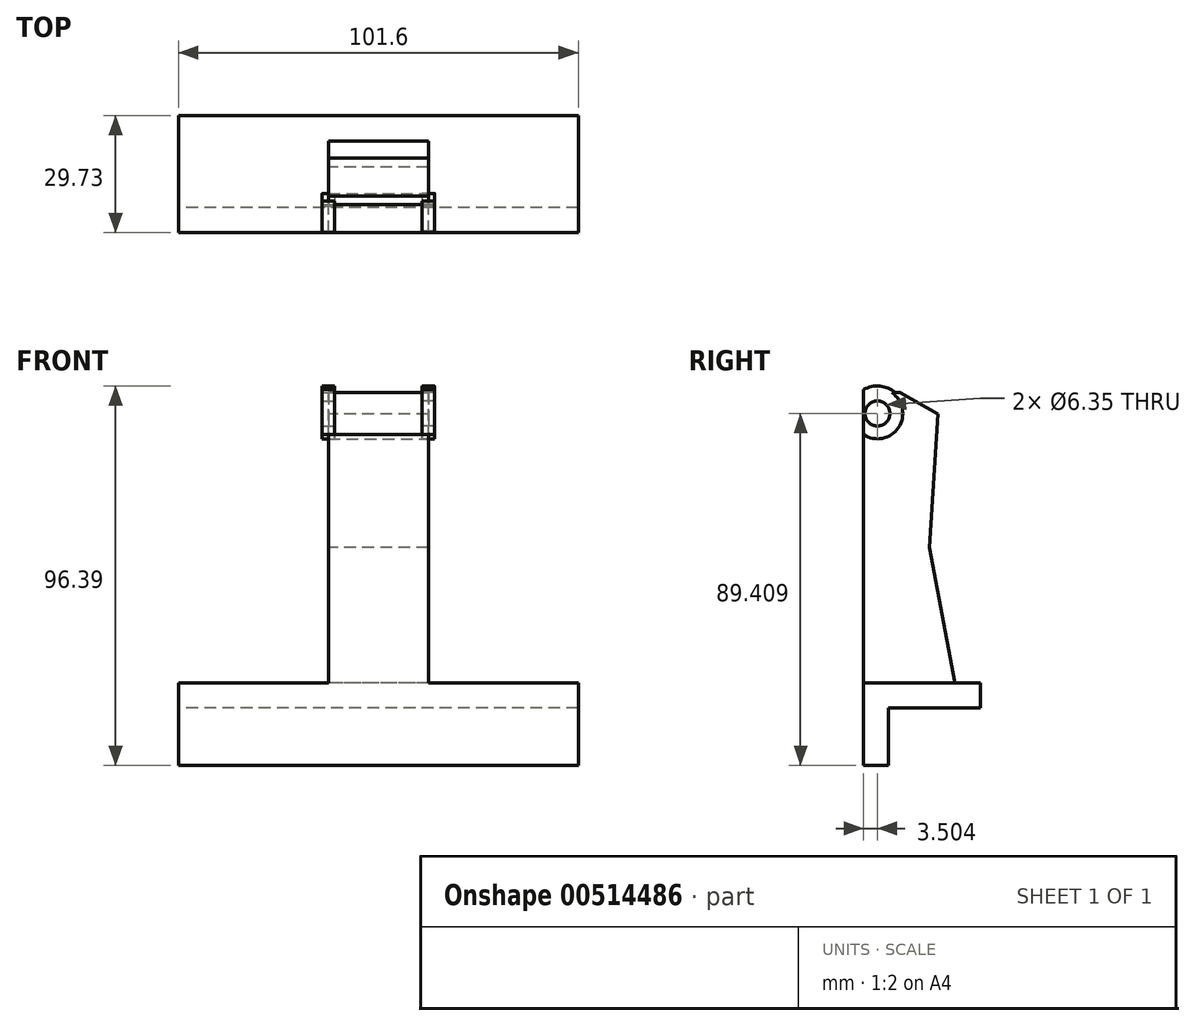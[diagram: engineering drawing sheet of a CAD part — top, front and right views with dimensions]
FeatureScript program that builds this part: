
annotation { "Feature Type Name" : "Feature", "Feature Type Description" : "" }
export const myFeature = defineFeature(function(context is Context, id is Id, definition is map)
    precondition{}
    {
        {
            var Q0;
            Q0=qCreatedBy(makeId("Right.planeOp"),FACE);
            var sketch = newSketch(context, id + "F0", { "sketchPlane" : qUnion([Q0])});
            skLineSegment(sketch, "E0.bottom", {"start": v(0, 0) * mm, "end": v(6.35, 0) * mm});
            skLineSegment(sketch, "E0.left", {"start": v(0, 0) * mm, "end": v(0, 20.91) * mm});
            skLineSegment(sketch, "E0.right", {"start": v(6.35, 0) * mm, "end": v(6.35, 14.56) * mm});
            skLineSegment(sketch, "E1.top", {"start": v(6.35, 14.56) * mm, "end": v(23.38, 14.56) * mm});
            skLineSegment(sketch, "E1.left", {"start": v(0, 20.91) * mm, "end": v(0, 14.56) * mm});
            skLineSegment(sketch, "E1.right", {"start": v(23.38, 20.91) * mm, "end": v(23.38, 14.56) * mm});
            skLineSegment(sketch, "E2.bottom", {"start": v(12.7, 14.56) * mm, "end": v(6.35, 14.56) * mm});
            skLineSegment(sketch, "E2.top", {"start": v(12.7, 101.1) * mm, "end": v(0, 101.1) * mm});
            skLineSegment(sketch, "E2.right", {"start": v(0, 20.91) * mm, "end": v(0, 101.1) * mm});
            skLineSegment(sketch, "E3", {"start": v(12.7, 65.87) * mm, "end": v(23.38, 20.91) * mm});
            skLineSegment(sketch, "E4", {"start": v(0, 20.91) * mm, "end": v(23.38, 20.91) * mm});
            skLineSegment(sketch, "E5", {"start": v(12.7, 101.1) * mm, "end": v(19.3, 97.56) * mm});
            skLineSegment(sketch, "E6", {"start": v(19.3, 97.56) * mm, "end": v(19.3, 74.64) * mm});
            skLineSegment(sketch, "E7", {"start": v(19.3, 74.64) * mm, "end": v(12.7, 65.87) * mm});
            skSolve(sketch);
        }
        {
            var Q0;
            Q0=makeQuery(id+"F0.imprint","IMPRINT",FACE,{"disambiguationData":[TD([[makeQuery(id+"F0.imprint","IMPRINT",EDGE,{"derivedFrom":sQuery(id+"F0.wireOp",EDGE,"E0.bottom")}),1.0]])]});
            extrude(context, id + "F1", {"entities" : qUnion([Q0]), "depth" : 101.6 * mm});
        }
        {
            var Q0;
            Q0=makeQuery(id+"F1.opExtrude","CAP_FACE",FACE,{"disambiguationData":[OSD([sQuery(id+"F0.wireOp",EDGE,"E0.bottom"),sQuery(id+"F0.wireOp",EDGE,"E0.left"),sQuery(id+"F0.wireOp",EDGE,"E0.right"),sQuery(id+"F0.wireOp",EDGE,"E1.top"),sQuery(id+"F0.wireOp",EDGE,"E1.left"),sQuery(id+"F0.wireOp",EDGE,"E1.right"),sQuery(id+"F0.wireOp",EDGE,"E2.bottom"),sQuery(id+"F0.wireOp",EDGE,"E4")])],"isStart":false});
            cPlane(context, id + "F2", {"entities" : qUnion([Q0]), "cplaneType" : CPlaneType.OFFSET, "offset" : 50.8 * mm, "oppositeDirection" : true, "width" : 152.4 * mm, "height" : 152.4 * mm});
        }
        {
            var Q0;
            Q0=qCreatedBy(id+"F2.planeOp",FACE);
            var sketch = newSketch(context, id + "F3", { "sketchPlane" : qUnion([Q0])});
            skLineSegment(sketch, "E8", {"start": v(0, 18.54) * mm, "end": v(0, 94.71) * mm});
            skLineSegment(sketch, "E9", {"start": v(0, 94.71) * mm, "end": v(9.23, 94.71) * mm});
            skLineSegment(sketch, "E10", {"start": v(16.68, 55.42) * mm, "end": v(23.22, 20.92) * mm});
            skLineSegment(sketch, "E11", {"start": v(23.22, 20.92) * mm, "end": v(19.9, 16.72) * mm});
            skLineSegment(sketch, "E12", {"start": v(19.9, 16.72) * mm, "end": v(0, 18.54) * mm});
            skLineSegment(sketch, "E13", {"start": v(9.23, 94.71) * mm, "end": v(18.9, 89.31) * mm});
            skLineSegment(sketch, "E14", {"start": v(18.9, 89.31) * mm, "end": v(16.68, 55.42) * mm});
            skSolve(sketch);
        }
        {
            var Q0;
            Q0=makeQuery(id+"F3.imprint","IMPRINT",FACE,{"disambiguationData":[TD([[makeQuery(id+"F3.imprint","IMPRINT",EDGE,{"derivedFrom":sQuery(id+"F3.wireOp",EDGE,"E8")}),-1.0]])]});
            extrude(context, id + "F4", {"entities" : qUnion([Q0]), "operationType" : NewBodyOperationType.ADD, "depth" : 12.7 * mm, "hasSecondDirection" : true, "secondDirectionOppositeDirection" : true, "secondDirectionDepth" : 12.7 * mm});
        }
        {
            var Q0;
            Q0=makeQuery(id+"F4.opExtrude","CAP_FACE",FACE,{"disambiguationData":[OSD([sQuery(id+"F3.wireOp",EDGE,"E8"),sQuery(id+"F3.wireOp",EDGE,"E9"),sQuery(id+"F3.wireOp",EDGE,"E10"),sQuery(id+"F3.wireOp",EDGE,"E11"),sQuery(id+"F3.wireOp",EDGE,"E12")])],"isStart":false});
            var sketch = newSketch(context, id + "F5", { "sketchPlane" : qUnion([Q0])});
            skCircle(sketch, "E15", {"center": v(3.5, 89.4) * mm, "radius": 6.43 * mm});
            skSolve(sketch);
        }
        {
            var Q0;
            {var subQ0=sQuery(id+"F5.wireOp",EDGE,"E15");var subQ1=makeQuery(id+"F4.opExtrude","CAP_EDGE",EDGE,{"disambiguationData":[OSD([sQuery(id+"F3.wireOp",EDGE,"E9")])],"isStart":false});var subQ2=makeQuery(id+"F5.imprint","INTERSECT",VERTEX,{"derivedFrom":[subQ1,subQ0]});Q0=makeQuery(id+"F5.imprint","IMPRINT",FACE,{"disambiguationData":[TD([[makeQuery(id+"F5.imprint","IMPRINT",EDGE,{"disambiguationData":[TD([[subQ2,-1.0]])],"derivedFrom":subQ0}),1.0]])]});}
            var Q1;
            {var subQ0=sQuery(id+"F5.wireOp",EDGE,"E15");var subQ1=makeQuery(id+"F4.opExtrude","CAP_EDGE",EDGE,{"disambiguationData":[OSD([sQuery(id+"F3.wireOp",EDGE,"E9")])],"isStart":false});var subQ2=makeQuery(id+"F5.imprint","INTERSECT",VERTEX,{"derivedFrom":[subQ1,subQ0]});Q1=makeQuery(id+"F5.imprint","IMPRINT",FACE,{"disambiguationData":[TD([[makeQuery(id+"F5.imprint","IMPRINT",EDGE,{"disambiguationData":[TD([[subQ2,1.0]])],"derivedFrom":subQ0}),1.0]])]});}
            extrude(context, id + "F6", {"entities" : qUnion([Q0, Q1]), "operationType" : NewBodyOperationType.REMOVE, "oppositeDirection" : true, "depth" : 25.4 * mm});
        }
        {
            var Q0;
            Q0=makeQuery(id+"F1.opExtrude","SWEPT_FACE",FACE,{"disambiguationData":[OSD([sQuery(id+"F0.wireOp",EDGE,"E1.right")])]});
            extrude(context, id + "F7", {"entities" : qUnion([Q0]), "operationType" : NewBodyOperationType.ADD, "depth" : 6.35 * mm});
        }
        {
            var Q0;
            Q0=makeQuery(id+"F4.opExtrude","CAP_FACE",FACE,{"disambiguationData":[OSD([sQuery(id+"F3.wireOp",EDGE,"E8"),sQuery(id+"F3.wireOp",EDGE,"E9"),sQuery(id+"F3.wireOp",EDGE,"E10"),sQuery(id+"F3.wireOp",EDGE,"E11"),sQuery(id+"F3.wireOp",EDGE,"E12"),sQuery(id+"F3.wireOp",EDGE,"E13"),sQuery(id+"F3.wireOp",EDGE,"E14")])],"isStart":false});
            var sketch = newSketch(context, id + "F8", { "sketchPlane" : qUnion([Q0])});
            skCircle(sketch, "E16", {"center": v(3.5, 89.4) * mm, "radius": 6.99 * mm});
            skCircle(sketch, "E17", {"center": v(3.5, 89.4) * mm, "radius": 3.18 * mm});
            skSolve(sketch);
        }
        {
            var Q0;
            Q0=makeQuery(id+"F4.opExtrude","CAP_FACE",FACE,{"disambiguationData":[OSD([sQuery(id+"F3.wireOp",EDGE,"E8"),sQuery(id+"F3.wireOp",EDGE,"E9"),sQuery(id+"F3.wireOp",EDGE,"E10"),sQuery(id+"F3.wireOp",EDGE,"E11"),sQuery(id+"F3.wireOp",EDGE,"E12"),sQuery(id+"F3.wireOp",EDGE,"E13"),sQuery(id+"F3.wireOp",EDGE,"E14")])],"isStart":true});
            var sketch = newSketch(context, id + "F9", { "sketchPlane" : qUnion([Q0])});
            skCircle(sketch, "E18", {"center": v(-3.5, 89.4) * mm, "radius": 6.98 * mm});
            skCircle(sketch, "E19", {"center": v(-3.5, 89.4) * mm, "radius": 3.18 * mm});
            skSolve(sketch);
        }
        {
            var Q0;
            Q0=makeQuery(id+"F9.imprint","IMPRINT",FACE,{"disambiguationData":[TD([[makeQuery(id+"F9.imprint","IMPRINT",EDGE,{"derivedFrom":sQuery(id+"F9.wireOp",EDGE,"E19")}),-1.0]])]});
            extrude(context, id + "F10", {"entities" : qUnion([Q0]), "endBound" : BoundingType.SYMMETRIC, "depth" : 3.17 * mm, "offsetDistance" : 25.4 * mm});
        }
        {
            var Q0;
            Q0=makeQuery(id+"F8.imprint","IMPRINT",FACE,{"disambiguationData":[TD([[makeQuery(id+"F8.imprint","IMPRINT",EDGE,{"derivedFrom":sQuery(id+"F8.wireOp",EDGE,"E17")}),-1.0]])]});
            extrude(context, id + "F11", {"entities" : qUnion([Q0]), "endBound" : BoundingType.SYMMETRIC, "depth" : 3.17 * mm, "offsetDistance" : 25.4 * mm});
        }
        {
            var Q0;
            {var subQ0=sQuery(id+"F0.wireOp",EDGE,"E1.right");Q0=makeQuery(id+"F7.boolean.opBoolean","MERGE",FACE,{"derivedFrom":[makeQuery(id+"F1.opExtrude","CAP_FACE",FACE,{"disambiguationData":[OSD([sQuery(id+"F0.wireOp",EDGE,"E0.bottom"),sQuery(id+"F0.wireOp",EDGE,"E0.left"),sQuery(id+"F0.wireOp",EDGE,"E0.right"),sQuery(id+"F0.wireOp",EDGE,"E1.top"),sQuery(id+"F0.wireOp",EDGE,"E1.left"),subQ0,sQuery(id+"F0.wireOp",EDGE,"E2.bottom"),sQuery(id+"F0.wireOp",EDGE,"E4")])],"isStart":false}),makeQuery(id+"F7.opExtrude","SWEPT_FACE",FACE,{"disambiguationData":[OSD([subQ0]),TDD([makeQuery(id+"F1.opExtrude","CAP_EDGE",EDGE,{"disambiguationData":[OSD([subQ0])],"isStart":false})])]})]});}
            var sketch = newSketch(context, id + "F12", { "sketchPlane" : qUnion([Q0])});
            skLineSegment(sketch, "E20.bottom", {"start": v(0, 67.9) * mm, "end": v(-12.88, 67.9) * mm});
            skLineSegment(sketch, "E20.top", {"start": v(0, 98.76) * mm, "end": v(-12.88, 98.76) * mm});
            skLineSegment(sketch, "E20.left", {"start": v(0, 67.9) * mm, "end": v(0, 98.76) * mm});
            skLineSegment(sketch, "E20.right", {"start": v(-12.88, 67.9) * mm, "end": v(-12.88, 98.76) * mm});
            skSolve(sketch);
        }
        {
            var Q0;
            Q0=makeQuery(id+"F12.imprint","IMPRINT",FACE,{"disambiguationData":[TD([[makeQuery(id+"F12.imprint","IMPRINT",EDGE,{"derivedFrom":sQuery(id+"F12.wireOp",EDGE,"E20.bottom")}),-1.0]])]});
            extrude(context, id + "F13", {"entities" : qUnion([Q0]), "operationType" : NewBodyOperationType.REMOVE, "oppositeDirection" : true, "depth" : 127 * mm, "offsetDistance" : 25.4 * mm});
        }
    });
